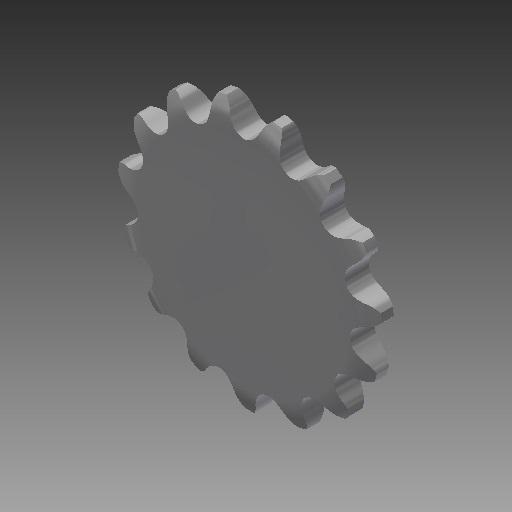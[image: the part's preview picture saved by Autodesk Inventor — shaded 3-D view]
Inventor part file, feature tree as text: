
AUTODESK INVENTOR PART (.ipt)
format: ipt  version: 2017 (Build 210142000, 142)  size: 507,392 bytes
history: native  units: mm
features: other x6, extrude x2, pattern_linear x1, pattern_circular x1
ambient origin geometry x8: Origin, YZ Plane, XZ Plane, XY Plane, X Axis, Y Axis, Z Axis, Center Point
bodies: Solid1 (feature_tree)
feature tree (10):
  other  "Theoretical Tooth Profile"
  other  "Tooth Profile"
  other  "Section Profile"
  other  "Shroud"
  other  "Strand"
  pattern_linear  "Strand Pattern"  Spacing1=30.541813mm  [1 undecoded]
  extrude  "Theoretical Tooth"  Depth=4.18879mm
  extrude  "Tooth"  Depth=1.697355mm
  pattern_circular  "Tooth Pattern"  [2 undecoded]
  other  "Timing Plane"
note: 3 required parameter values undecoded (feature->parameter linkage not recoverable at this tier; creation-order binding heuristic only, values carry confidence <= 0.55)
